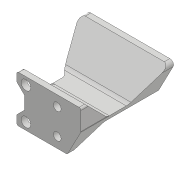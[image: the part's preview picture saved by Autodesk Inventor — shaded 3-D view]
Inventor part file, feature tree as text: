
AUTODESK INVENTOR PART (.ipt)
format: ipt  version: 2018 (Build 220112000, 112)  size: 605,696 bytes
history: native  units: mm
features: sketch x15, extrude x12, projected_geometry x10, fillet x5, hole x4, chamfer x3, plane x1, mirror x1
ambient origin geometry x8: Origin, YZ Plane, XZ Plane, XY Plane, X Axis, Y Axis, Z Axis, Center Point
bodies: Solid1 (feature_tree)
feature tree (51):
  extrude  "Extrusion1"  Depth=143.6mm
  hole  "Hole1"  [1 undecoded]
  extrude  "Extrusion2"  Depth=40.0mm
  extrude  "Extrusion5"  Depth=2.0mm
  extrude  "Extrusion3"  Depth=3.0mm TaperAngle=0.0deg
  extrude  "Extrusion4"  Depth=3.0mm TaperAngle=0.0deg
  sketch  "Sketch8"  dims[d18=41.0mm d20=3.0mm d21=0.0mm]
  hole  "Hole2"  [1 undecoded]
  hole  "Hole3"  [1 undecoded]
  extrude  "Extrusion6"  Depth=17.0624mm
  extrude  "Extrusion7"  Depth=2.0mm
  extrude  "Extrusion10"  Depth=3.0mm TaperAngle=0.0deg
  chamfer  "Chamfer3"  Distance=7.0mm
  plane  "Work Plane1"
  extrude  "Extrusion11"  Depth=2.0mm
  fillet  "Fillet1"  Radius=4.957359mm
  extrude  "Extrusion12"  Depth=2.0mm TaperAngle=0.0deg
  chamfer  "Chamfer4"  Distance=4.957359mm
  chamfer  "Chamfer5"  [1 undecoded]
  fillet  "Fillet2"  Radius=11.2mm
  fillet  "Fillet3"  Radius=10.0mm
  extrude  "Extrusion13"  [1 undecoded]
  fillet  "Fillet4"  Radius=8.0mm
  hole  "Hole4"  [1 undecoded]
  mirror  "Mirror2"
  extrude  "Extrusion14"  Depth=2.0mm
  fillet  "Fillet5"  Radius=9.5mm
  sketch  "Sketch1"  dims[d0=76.0mm d1=143.6mm]
  sketch  "Sketch2"  dims[d2=3.0mm d3=0.0mm d4=8.0mm]
  sketch  "Sketch4"  dims[d5=70.0mm d6=40.0mm]
  sketch  "Sketch5"  dims[d7=3.2mm d8=6.0mm d9=6.3mm d10=2.0mm d11=90.0deg d12=8.0mm d13=20.594885mm d14=38.0mm]
  projected_geometry  "Projected Loop1"
  sketch  "Sketch7"  dims[d15=17.0mm d16=3.0mm d17=0.0mm]
  projected_geometry  "Projected Loop3"
  projected_geometry  "Projected Loop4"
  sketch  "Sketch10"  dims[d22=25.4mm d23=3.0mm d24=0.0mm]
  projected_geometry  "Projected Loop5"
  sketch  "Sketch11"  dims[d25=14.0mm d26=12.7mm]
  projected_geometry  "Projected Loop6"
  sketch  "Sketch12"  dims[d27=17.4625mm d30=17.0624mm]
  projected_geometry  "Projected Loop7"
  sketch  "Sketch16"  dims[d31=5.0mm]
  projected_geometry  "Projected Loop11"
  projected_geometry  "Projected Loop12"
  sketch  "Sketch17"  dims[d32=4.3mm d33=6.0mm d34=9.4mm d35=2.0mm d36=90.0deg d37=8.0mm d38=20.594885mm]
  projected_geometry  "Projected Loop13"
  sketch  "Sketch18"  dims[d39=5.3mm d40=6.0mm d41=10.4mm d42=2.0mm d43=90.0deg d44=8.0mm d45=20.594885mm d46=46.0mm]
  projected_geometry  "Projected Loop14"
  sketch  "Sketch19"  dims[d47=24.0mm d48=3.0mm d49=0.0mm]
  sketch  "Sketch20"  dims[d50=135.0deg]
  sketch  "Sketch21"  dims[d51=135.0deg d52=7.0mm d53=6.0mm d54=4.957359mm d55=50.0mm d56=0.0mm d57=4.957359mm d58=0.0mm d59=0.0mm d71=11.2mm d72=0.0mm d73=11.2mm d74=10.0mm d75=45.0deg d76=-18.0mm d77=8.0mm d78=8.0mm d79=9.5mm d80=9.5mm d81=15.0mm d82=0.0mm d83=2.0mm d84=18.0mm d85=15.0mm d86=0.0mm d87=15.0mm d88=10.0mm d89=45.0deg d90=4.24mm d91=10.0mm d92=45.0deg d93=1.0mm d94=3.0mm d95=15.0mm d96=0.0mm d97=1.0mm d98=26.0mm d99=10.0mm d100=12.0mm d101=2.459mm d102=6.0mm d103=10.4mm d104=2.0mm d105=90.0deg d106=10.0mm d107=20.594885mm d108=10.0mm d109=0.0mm d110=2.0mm]
note: 6 required parameter values undecoded (feature->parameter linkage not recoverable at this tier; creation-order binding heuristic only, values carry confidence <= 0.55)
